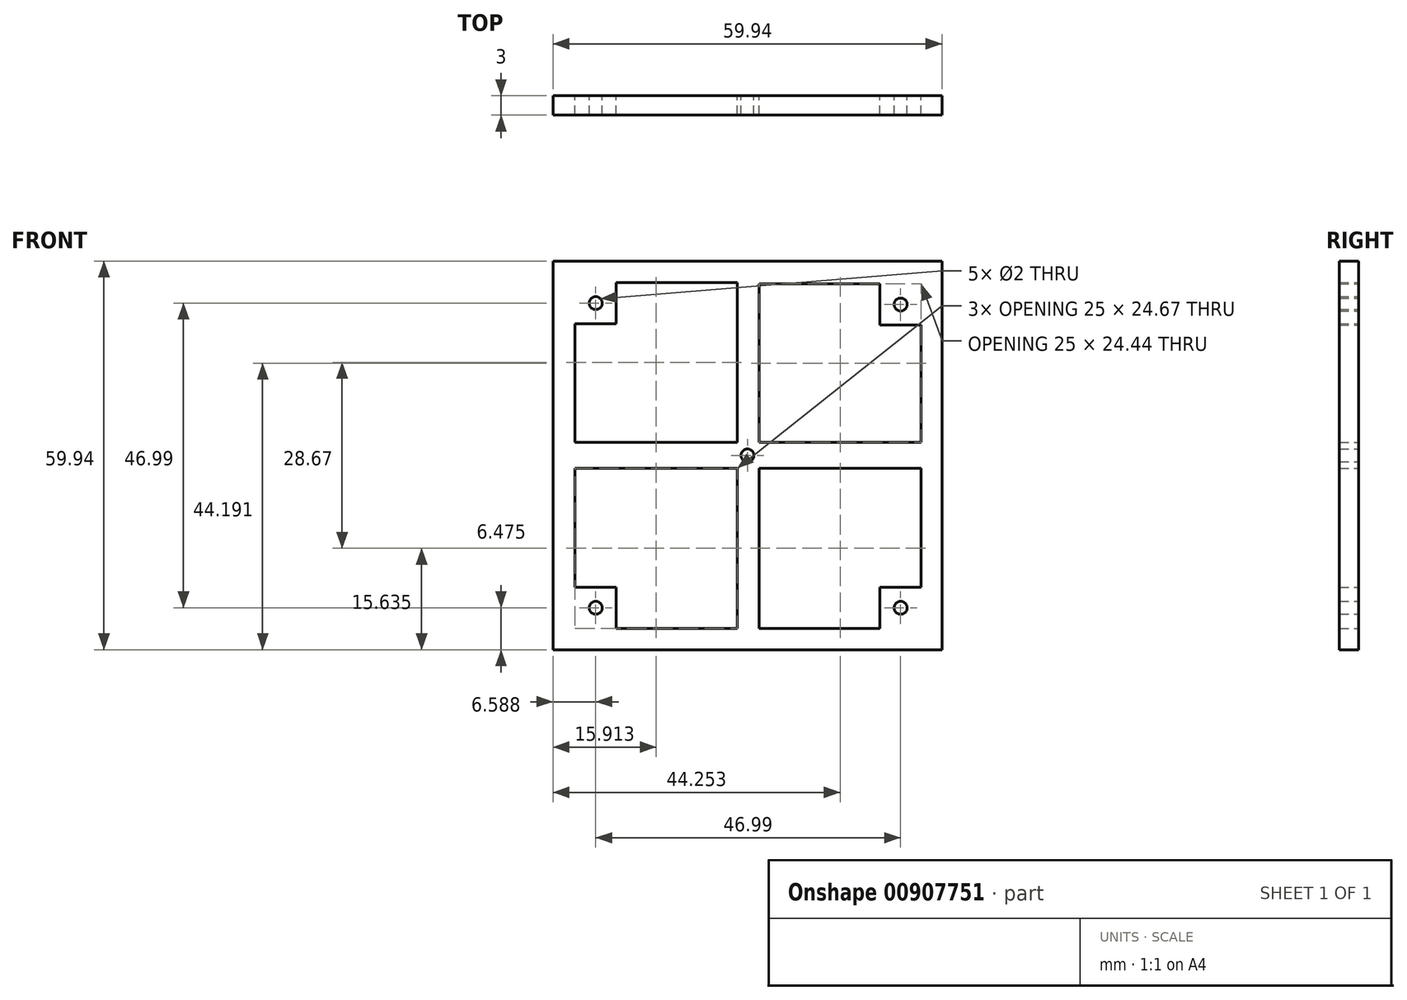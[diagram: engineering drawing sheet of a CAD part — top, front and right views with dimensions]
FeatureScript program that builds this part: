
annotation { "Feature Type Name" : "Feature", "Feature Type Description" : "" }
export const myFeature = defineFeature(function(context is Context, id is Id, definition is map)
    precondition{}
    {
        {
            var Q0;
            Q0=qCreatedBy(makeId("Front.planeOp"),FACE);
            var sketch = newSketch(context, id + "F0", { "sketchPlane" : qUnion([Q0])});
            skLineSegment(sketch, "E0.bottom", {"start": v(29.97, 29.97) * mm, "end": v(-29.97, 29.97) * mm});
            skLineSegment(sketch, "E0.top", {"start": v(29.97, -29.97) * mm, "end": v(-29.97, -29.97) * mm});
            skLineSegment(sketch, "E0.left", {"start": v(29.97, 29.97) * mm, "end": v(29.97, -29.97) * mm});
            skLineSegment(sketch, "E0.right", {"start": v(-29.97, 29.97) * mm, "end": v(-29.97, -29.97) * mm});
            skPoint(sketch, "E0.middle", {"position": v(0, 0) * mm});
            skPoint(sketch, "E1", {"position": v(-23.38, 23.5) * mm});
            skPoint(sketch, "E2", {"position": v(23.6, 23.27) * mm});
            skPoint(sketch, "E3", {"position": v(23.6, -23.5) * mm});
            skPoint(sketch, "E4", {"position": v(-23.38, -23.5) * mm});
            skLineSegment(sketch, "E5.bottom", {"start": v(-20.2, 26.67) * mm, "end": v(-26.56, 26.67) * mm});
            skLineSegment(sketch, "E5.top", {"start": v(-20.2, 20.32) * mm, "end": v(-26.56, 20.32) * mm});
            skLineSegment(sketch, "E5.left", {"start": v(-20.2, 26.67) * mm, "end": v(-20.2, 20.32) * mm});
            skLineSegment(sketch, "E5.right", {"start": v(-26.56, 26.67) * mm, "end": v(-26.56, 20.32) * mm});
            skLineSegment(sketch, "E6.bottom", {"start": v(26.78, 26.44) * mm, "end": v(20.43, 26.44) * mm});
            skLineSegment(sketch, "E6.top", {"start": v(26.78, 20.1) * mm, "end": v(20.43, 20.1) * mm});
            skLineSegment(sketch, "E6.left", {"start": v(26.78, 26.44) * mm, "end": v(26.78, 20.1) * mm});
            skLineSegment(sketch, "E6.right", {"start": v(20.43, 26.44) * mm, "end": v(20.43, 20.1) * mm});
            skLineSegment(sketch, "E7.bottom", {"start": v(26.78, -20.32) * mm, "end": v(20.43, -20.32) * mm});
            skLineSegment(sketch, "E7.top", {"start": v(26.78, -26.67) * mm, "end": v(20.43, -26.67) * mm});
            skLineSegment(sketch, "E7.left", {"start": v(26.78, -20.32) * mm, "end": v(26.78, -26.67) * mm});
            skLineSegment(sketch, "E7.right", {"start": v(20.43, -20.32) * mm, "end": v(20.43, -26.67) * mm});
            skLineSegment(sketch, "E8.bottom", {"start": v(-20.2, -20.32) * mm, "end": v(-26.56, -20.32) * mm});
            skLineSegment(sketch, "E8.top", {"start": v(-20.2, -26.67) * mm, "end": v(-26.56, -26.67) * mm});
            skLineSegment(sketch, "E8.left", {"start": v(-20.2, -20.32) * mm, "end": v(-20.2, -26.67) * mm});
            skLineSegment(sketch, "E8.right", {"start": v(-26.56, -20.32) * mm, "end": v(-26.56, -26.67) * mm});
            skLineSegment(sketch, "E9.bottom", {"start": v(26.78, -20.32) * mm, "end": v(1.78, -20.32) * mm});
            skLineSegment(sketch, "E9.top", {"start": v(26.78, 20.1) * mm, "end": v(1.78, 20.1) * mm});
            skLineSegment(sketch, "E9.left", {"start": v(26.78, -20.32) * mm, "end": v(26.78, 20.1) * mm});
            skLineSegment(sketch, "E9.right", {"start": v(1.78, -20.32) * mm, "end": v(1.78, 20.1) * mm});
            skLineSegment(sketch, "E10.bottom", {"start": v(-26.56, 20.32) * mm, "end": v(-1.56, 20.32) * mm});
            skLineSegment(sketch, "E10.top", {"start": v(-26.56, -20.32) * mm, "end": v(-1.56, -20.32) * mm});
            skLineSegment(sketch, "E10.left", {"start": v(-26.56, 20.32) * mm, "end": v(-26.56, -20.32) * mm});
            skLineSegment(sketch, "E10.right", {"start": v(-1.56, 20.32) * mm, "end": v(-1.56, -20.32) * mm});
            skLineSegment(sketch, "E11.left", {"start": v(20.43, 26.44) * mm, "end": v(20.43, 20.32) * mm});
            skLineSegment(sketch, "E11.right", {"start": v(-20.2, 26.44) * mm, "end": v(-20.2, 20.32) * mm});
            skLineSegment(sketch, "E12.bottom", {"start": v(20.43, -20.32) * mm, "end": v(1.78, -20.32) * mm});
            skLineSegment(sketch, "E12.top", {"start": v(20.43, -26.67) * mm, "end": v(1.78, -26.67) * mm});
            skLineSegment(sketch, "E12.right", {"start": v(1.78, -20.32) * mm, "end": v(1.78, -26.67) * mm});
            skLineSegment(sketch, "E13.bottom", {"start": v(-1.56, -20.32) * mm, "end": v(-20.2, -20.32) * mm});
            skLineSegment(sketch, "E13.top", {"start": v(-1.56, -26.67) * mm, "end": v(-20.2, -26.67) * mm});
            skLineSegment(sketch, "E13.left", {"start": v(-1.56, -20.32) * mm, "end": v(-1.56, -26.67) * mm});
            skLineSegment(sketch, "E14.bottom", {"start": v(20.43, 26.44) * mm, "end": v(1.78, 26.44) * mm});
            skLineSegment(sketch, "E14.top", {"start": v(20.43, 20.1) * mm, "end": v(1.78, 20.1) * mm});
            skLineSegment(sketch, "E14.right", {"start": v(1.78, 26.44) * mm, "end": v(1.78, 20.1) * mm});
            skLineSegment(sketch, "E15.bottom", {"start": v(-1.56, 20.32) * mm, "end": v(-20.2, 20.32) * mm});
            skLineSegment(sketch, "E15.top", {"start": v(-1.56, 26.67) * mm, "end": v(-20.2, 26.67) * mm});
            skLineSegment(sketch, "E15.left", {"start": v(-1.56, 20.32) * mm, "end": v(-1.56, 26.67) * mm});
            skLineSegment(sketch, "E15.right", {"start": v(-20.2, 20.32) * mm, "end": v(-20.2, 26.67) * mm});
            skLineSegment(sketch, "E16.bottom", {"start": v(1.78, 0) * mm, "end": v(26.78, 0) * mm});
            skLineSegment(sketch, "E16.top", {"start": v(1.78, 2) * mm, "end": v(26.78, 2) * mm});
            skLineSegment(sketch, "E16.left", {"start": v(1.78, 0) * mm, "end": v(1.78, 2) * mm});
            skLineSegment(sketch, "E16.right", {"start": v(26.78, 0) * mm, "end": v(26.78, 2) * mm});
            skLineSegment(sketch, "E17.top", {"start": v(1.78, -2) * mm, "end": v(26.78, -2) * mm});
            skLineSegment(sketch, "E17.left", {"start": v(1.78, 0) * mm, "end": v(1.78, -2) * mm});
            skLineSegment(sketch, "E17.right", {"start": v(26.78, 0) * mm, "end": v(26.78, -2) * mm});
            skLineSegment(sketch, "E18.bottom", {"start": v(-1.56, 0) * mm, "end": v(-26.56, 0) * mm});
            skLineSegment(sketch, "E18.top", {"start": v(-1.56, 2) * mm, "end": v(-26.56, 2) * mm});
            skLineSegment(sketch, "E18.left", {"start": v(-1.56, 0) * mm, "end": v(-1.56, 2) * mm});
            skLineSegment(sketch, "E18.right", {"start": v(-26.56, 0) * mm, "end": v(-26.56, 2) * mm});
            skLineSegment(sketch, "E19.bottom", {"start": v(-26.56, 0) * mm, "end": v(-1.56, 0) * mm});
            skLineSegment(sketch, "E19.top", {"start": v(-26.56, -2) * mm, "end": v(-1.56, -2) * mm});
            skLineSegment(sketch, "E19.left", {"start": v(-26.56, 0) * mm, "end": v(-26.56, -2) * mm});
            skLineSegment(sketch, "E19.right", {"start": v(-1.56, 0) * mm, "end": v(-1.56, -2) * mm});
            skSolve(sketch);
        }
        {
            var Q0;
            Q0=makeQuery(id+"F0.imprint","IMPRINT",FACE,{"disambiguationData":[TD([[makeQuery(id+"F0.imprint","IMPRINT",EDGE,{"derivedFrom":sQuery(id+"F0.wireOp",EDGE,"gArEzE6q-VlUX-FMNO-9lor-69F1d1fahksi")}),-1.0]])]});
            var Q1;
            {var subQ1=sQuery(id+"F0.wireOp",EDGE,"E5.bottom");Q1=makeQuery(id+"F0.imprint","IMPRINT",FACE,{"disambiguationData":[TD([[makeQuery(id+"F0.imprint","IMPRINT",EDGE,{"derivedFrom":subQ1}),1.0]])]});}
            var Q2;
            {var subQ1=sQuery(id+"F0.wireOp",EDGE,"E6.bottom");Q2=makeQuery(id+"F0.imprint","IMPRINT",FACE,{"disambiguationData":[TD([[makeQuery(id+"F0.imprint","IMPRINT",EDGE,{"derivedFrom":subQ1}),1.0]])]});}
            var Q3;
            Q3=makeQuery(id+"F0.imprint","IMPRINT",FACE,{"disambiguationData":[TD([[makeQuery(id+"F0.imprint","IMPRINT",EDGE,{"derivedFrom":sQuery(id+"F0.wireOp",EDGE,"E7.bottom")}),1.0]])]});
            var Q4;
            Q4=makeQuery(id+"F0.imprint","IMPRINT",FACE,{"disambiguationData":[TD([[makeQuery(id+"F0.imprint","IMPRINT",EDGE,{"derivedFrom":sQuery(id+"F0.wireOp",EDGE,"E8.bottom")}),1.0]])]});
            var Q5;
            Q5=makeQuery(id+"F0.imprint","IMPRINT",FACE,{"disambiguationData":[TD([[makeQuery(id+"F0.imprint","IMPRINT",EDGE,{"derivedFrom":sQuery(id+"F0.wireOp",EDGE,"gArEzE6q-VlUX-FMNO-9lor-69F1d1fahksi")}),1.0]])]});
            var Q6;
            Q6=makeQuery(id+"F0.imprint","IMPRINT",FACE,{"disambiguationData":[TD([[makeQuery(id+"F0.imprint","IMPRINT",EDGE,{"derivedFrom":sQuery(id+"F0.wireOp",EDGE,"E0.bottom")}),1.0]])]});
            var Q7;
            Q7=makeQuery(id+"F0.imprint","IMPRINT",FACE,{"disambiguationData":[TD([[makeQuery(id+"F0.imprint","IMPRINT",EDGE,{"derivedFrom":sQuery(id+"F0.wireOp",EDGE,"E7.bottom")}),1.0]])]});
            var Q8;
            Q8=makeQuery(id+"F0.imprint","IMPRINT",FACE,{"disambiguationData":[TD([[makeQuery(id+"F0.imprint","IMPRINT",EDGE,{"derivedFrom":sQuery(id+"F0.wireOp",EDGE,"E8.bottom")}),1.0]])]});
            var Q9;
            {var subQ0=sQuery(id+"F0.wireOp",EDGE,"E16.bottom");Q9=makeQuery(id+"F0.imprint","IMPRINT",FACE,{"disambiguationData":[TD([[makeQuery(id+"F0.imprint","IMPRINT",EDGE,{"derivedFrom":subQ0}),1.0]])]});}
            var Q10;
            {var subQ0=sQuery(id+"F0.wireOp",EDGE,"E16.bottom");Q10=makeQuery(id+"F0.imprint","IMPRINT",FACE,{"disambiguationData":[TD([[makeQuery(id+"F0.imprint","IMPRINT",EDGE,{"derivedFrom":subQ0}),-1.0]])]});}
            var Q11;
            {var subQ0=sQuery(id+"F0.wireOp",EDGE,"E18.bottom");Q11=makeQuery(id+"F0.imprint","IMPRINT",FACE,{"disambiguationData":[TD([[makeQuery(id+"F0.imprint","IMPRINT",EDGE,{"derivedFrom":subQ0}),-1.0]])]});}
            var Q12;
            {var subQ0=sQuery(id+"F0.wireOp",EDGE,"E18.bottom");Q12=makeQuery(id+"F0.imprint","IMPRINT",FACE,{"disambiguationData":[TD([[makeQuery(id+"F0.imprint","IMPRINT",EDGE,{"derivedFrom":subQ0}),1.0]])]});}
            extrude(context, id + "F1", {"entities" : qUnion([Q0, Q1, Q2, Q3, Q4, Q5, Q6, Q7, Q8, Q9, Q10, Q11, Q12]), "depth" : 3 * mm, "offsetDistance" : 25 * mm});
        }
        {
            var Q0;
            Q0=sQuery(id+"F0.wireOp",VERTEX,"E2");
            var Q1;
            Q1=sQuery(id+"F0.wireOp",VERTEX,"E0.middle");
            var Q2;
            Q2=sQuery(id+"F0.wireOp",VERTEX,"E3");
            var Q3;
            Q3=sQuery(id+"F0.wireOp",VERTEX,"E1");
            var Q4;
            Q4=sQuery(id+"F0.wireOp",VERTEX,"E4");
            var Q5;
            Q5=makeQuery(id+"F1.opExtrude","SWEPT_BODY",BODY,{"disambiguationData":[OSD([sQuery(id+"F0.wireOp",EDGE,"E0.bottom"),sQuery(id+"F0.wireOp",EDGE,"E0.top"),sQuery(id+"F0.wireOp",EDGE,"E0.left"),sQuery(id+"F0.wireOp",EDGE,"E0.right"),sQuery(id+"F0.wireOp",EDGE,"E5.top"),sQuery(id+"F0.wireOp",EDGE,"E5.left"),sQuery(id+"F0.wireOp",EDGE,"E6.top"),sQuery(id+"F0.wireOp",EDGE,"E6.right"),sQuery(id+"F0.wireOp",EDGE,"E7.bottom"),sQuery(id+"F0.wireOp",EDGE,"E7.right"),sQuery(id+"F0.wireOp",EDGE,"E8.bottom"),sQuery(id+"F0.wireOp",EDGE,"E8.left"),sQuery(id+"F0.wireOp",EDGE,"E9.left"),sQuery(id+"F0.wireOp",EDGE,"E9.right"),sQuery(id+"F0.wireOp",EDGE,"E10.left"),sQuery(id+"F0.wireOp",EDGE,"E10.right"),sQuery(id+"F0.wireOp",EDGE,"E12.top"),sQuery(id+"F0.wireOp",EDGE,"E12.right"),sQuery(id+"F0.wireOp",EDGE,"E13.top"),sQuery(id+"F0.wireOp",EDGE,"E13.left"),sQuery(id+"F0.wireOp",EDGE,"E14.bottom"),sQuery(id+"F0.wireOp",EDGE,"E14.right"),sQuery(id+"F0.wireOp",EDGE,"E15.top"),sQuery(id+"F0.wireOp",EDGE,"E15.left"),sQuery(id+"F0.wireOp",EDGE,"E16.top"),sQuery(id+"F0.wireOp",EDGE,"E17.top"),sQuery(id+"F0.wireOp",EDGE,"E18.top"),sQuery(id+"F0.wireOp",EDGE,"E19.top")])]});
            hole(context, id + "F2", {"style" : HoleStyle.SIMPLE, "endStyle" : HoleEndStyle.THROUGH, "oppositeDirection" : true, "holeDiameter" : 2 * mm, "majorDiameter" : 5 * mm, "isTappedThrough" : true, "tappedDepth" : 12 * mm, "tapClearance" : 3, "locations" : qUnion([Q0, Q1, Q2, Q3, Q4]), "scope" : qUnion([Q5])});
        }
    });
